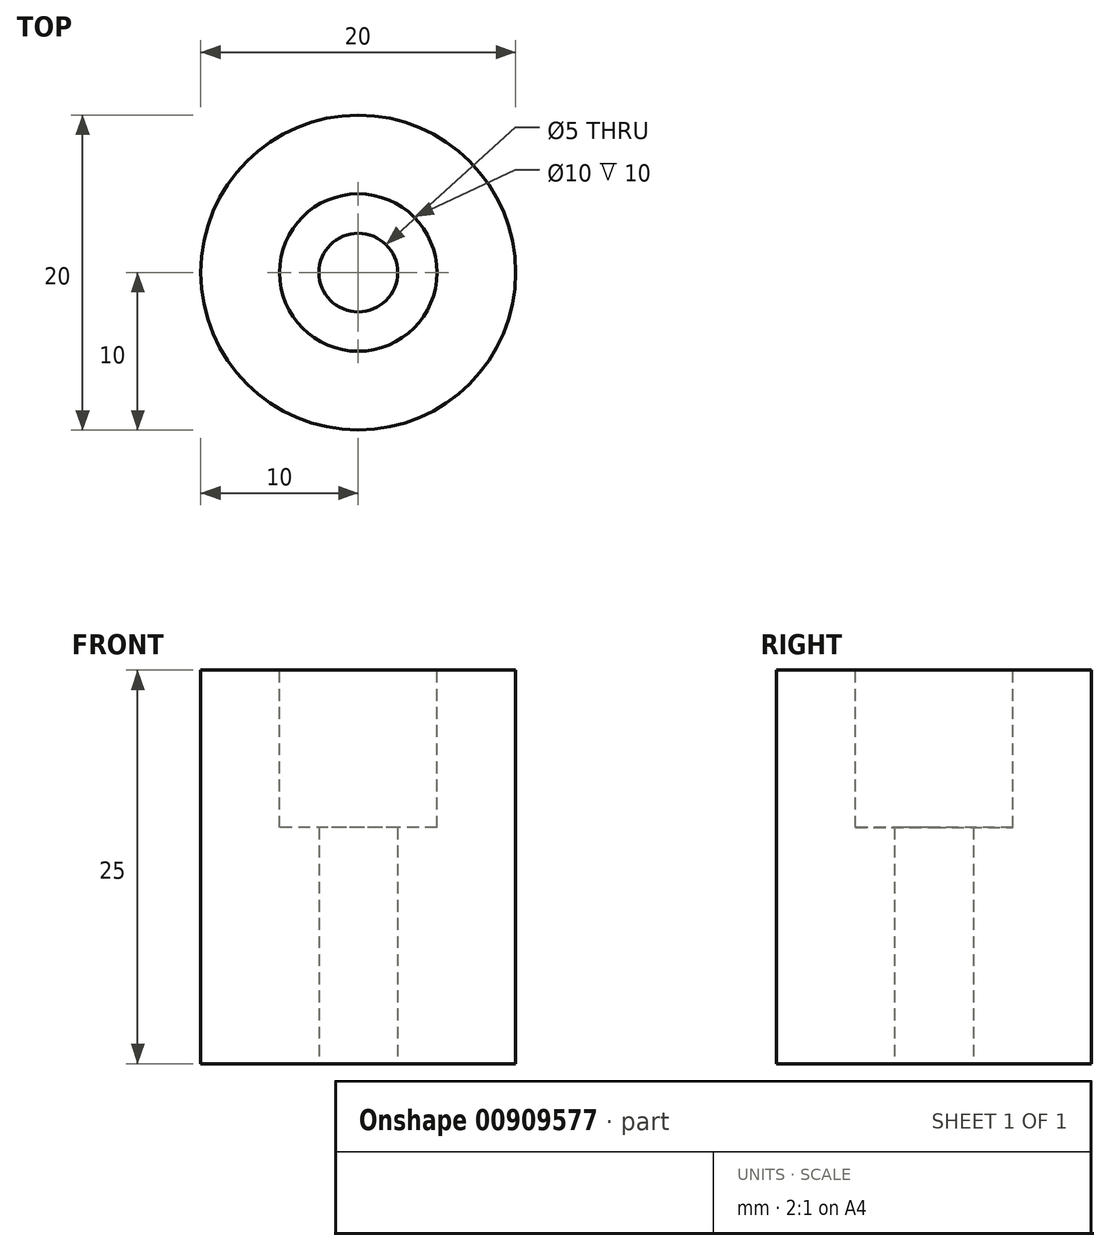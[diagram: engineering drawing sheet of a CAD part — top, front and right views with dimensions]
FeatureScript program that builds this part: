
annotation { "Feature Type Name" : "Feature", "Feature Type Description" : "" }
export const myFeature = defineFeature(function(context is Context, id is Id, definition is map)
    precondition{}
    {
        {
            var Q0;
            Q0=qCreatedBy(makeId("Top.planeOp"),FACE);
            var sketch = newSketch(context, id + "F0", { "sketchPlane" : qUnion([Q0])});
            skCircle(sketch, "E0", {"center": v(0, 0) * mm, "radius": 10 * mm});
            skSolve(sketch);
        }
        {
            var Q0;
            Q0=makeQuery(id+"F0.imprint","IMPRINT",FACE,{"disambiguationData":[TD([[makeQuery(id+"F0.imprint","IMPRINT",EDGE,{"derivedFrom":sQuery(id+"F0.wireOp",EDGE,"E0")}),1.0]])]});
            extrude(context, id + "F1", {"entities" : qUnion([Q0]), "depth" : 25 * mm, "offsetDistance" : 25.4 * mm});
        }
        {
            var Q0;
            Q0=makeQuery(id+"F1.opExtrude","CAP_FACE",FACE,{"disambiguationData":[OSD([sQuery(id+"F0.wireOp",EDGE,"E0")])],"isStart":false});
            var sketch = newSketch(context, id + "F2", { "sketchPlane" : qUnion([Q0])});
            skCircle(sketch, "E1", {"center": v(0, 0) * mm, "radius": 5 * mm});
            skSolve(sketch);
        }
        {
            var Q0;
            Q0=makeQuery(id+"F1.opExtrude","CAP_FACE",FACE,{"disambiguationData":[OSD([sQuery(id+"F0.wireOp",EDGE,"E0")])],"isStart":true});
            var sketch = newSketch(context, id + "F3", { "sketchPlane" : qUnion([Q0])});
            skCircle(sketch, "E2", {"center": v(0, 0) * mm, "radius": 2.5 * mm});
            skSolve(sketch);
        }
        {
            var Q0;
            Q0=makeQuery(id+"F3.imprint","IMPRINT",FACE,{"disambiguationData":[TD([[makeQuery(id+"F3.imprint","IMPRINT",EDGE,{"derivedFrom":sQuery(id+"F3.wireOp",EDGE,"E2")}),1.0]])]});
            extrude(context, id + "F4", {"entities" : qUnion([Q0]), "operationType" : NewBodyOperationType.REMOVE, "oppositeDirection" : true, "depth" : 25.4 * mm, "offsetDistance" : 25.4 * mm});
        }
        {
            var Q0;
            Q0=makeQuery(id+"F2.imprint","IMPRINT",FACE,{"disambiguationData":[TD([[makeQuery(id+"F2.imprint","IMPRINT",EDGE,{"derivedFrom":sQuery(id+"F2.wireOp",EDGE,"E1")}),1.0]])]});
            extrude(context, id + "F5", {"entities" : qUnion([Q0]), "operationType" : NewBodyOperationType.REMOVE, "oppositeDirection" : true, "depth" : 10 * mm, "offsetDistance" : 25.4 * mm});
        }
    });
